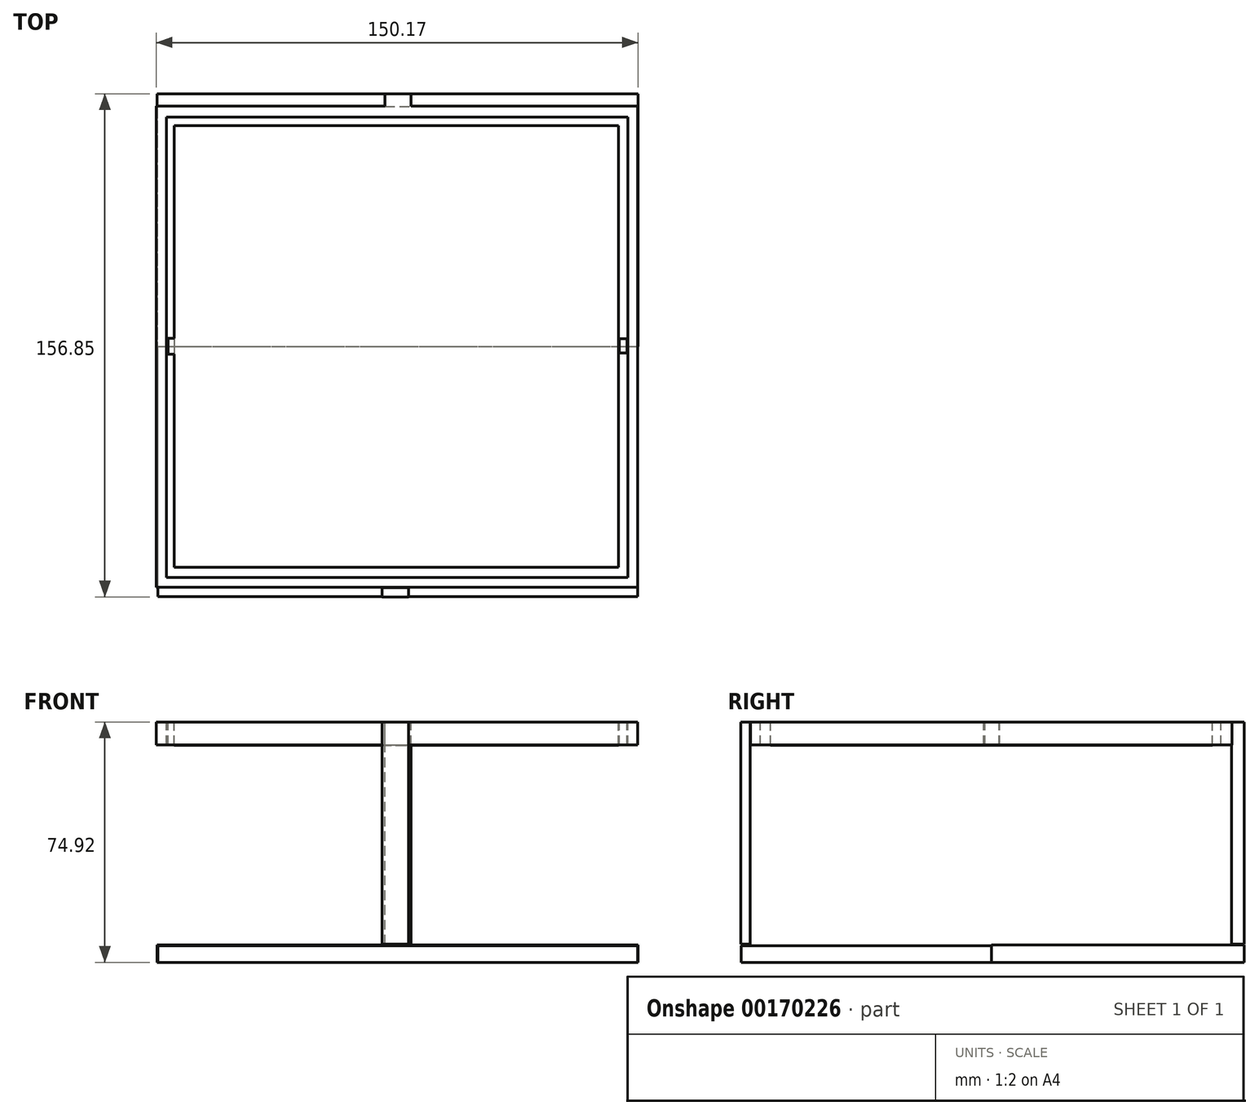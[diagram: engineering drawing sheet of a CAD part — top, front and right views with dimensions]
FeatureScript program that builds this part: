
annotation { "Feature Type Name" : "Feature", "Feature Type Description" : "" }
export const myFeature = defineFeature(function(context is Context, id is Id, definition is map)
    precondition{}
    {
        {
            var Q0;
            Q0=qCreatedBy(makeId("Top.planeOp"),FACE);
            var sketch = newSketch(context, id + "F0", { "sketchPlane" : qUnion([Q0])});
            skLineSegment(sketch, "E0.bottom", {"start": v(-75.11, 74.92) * mm, "end": v(74.92, 74.92) * mm});
            skLineSegment(sketch, "E0.top", {"start": v(-75.11, -75.11) * mm, "end": v(74.92, -75.11) * mm});
            skLineSegment(sketch, "E0.left", {"start": v(-75.11, 74.92) * mm, "end": v(-75.11, -75.11) * mm});
            skLineSegment(sketch, "E0.right", {"start": v(74.92, 74.92) * mm, "end": v(74.92, -75.11) * mm});
            skLineSegment(sketch, "E1.bottom", {"start": v(-71.86, 71.48) * mm, "end": v(71.86, 71.48) * mm});
            skLineSegment(sketch, "E1.top", {"start": v(-71.86, -72.05) * mm, "end": v(71.86, -72.05) * mm});
            skLineSegment(sketch, "E1.left", {"start": v(-71.86, 71.48) * mm, "end": v(-71.86, -72.05) * mm});
            skLineSegment(sketch, "E1.right", {"start": v(71.86, 71.48) * mm, "end": v(71.86, -72.05) * mm});
            skLineSegment(sketch, "E2.bottom", {"start": v(-68.8, 68.99) * mm, "end": v(69.37, 68.99) * mm});
            skLineSegment(sketch, "E2.top", {"start": v(-68.8, -69.18) * mm, "end": v(69.37, -69.18) * mm});
            skLineSegment(sketch, "E2.left", {"start": v(-68.8, 68.99) * mm, "end": v(-68.8, -69.18) * mm});
            skLineSegment(sketch, "E2.right", {"start": v(69.37, 68.99) * mm, "end": v(69.37, -69.18) * mm});
            skLineSegment(sketch, "E3.bottom", {"start": v(-2.58, 71.48) * mm, "end": v(2.58, 71.48) * mm});
            skLineSegment(sketch, "E3.top", {"start": v(-2.58, 68.99) * mm, "end": v(2.58, 68.99) * mm});
            skLineSegment(sketch, "E3.left", {"start": v(-2.58, 71.48) * mm, "end": v(-2.58, 68.99) * mm});
            skLineSegment(sketch, "E3.right", {"start": v(2.58, 71.48) * mm, "end": v(2.58, 68.99) * mm});
            skLineSegment(sketch, "E4.bottom", {"start": v(2.58, -69.18) * mm, "end": v(-2.58, -69.18) * mm});
            skLineSegment(sketch, "E4.top", {"start": v(2.58, -72.05) * mm, "end": v(-2.58, -72.05) * mm});
            skLineSegment(sketch, "E4.left", {"start": v(2.58, -69.18) * mm, "end": v(2.58, -72.05) * mm});
            skLineSegment(sketch, "E4.right", {"start": v(-2.58, -69.18) * mm, "end": v(-2.58, -72.05) * mm});
            skSolve(sketch);
        }
        {
            var Q0;
            Q0 = qSketchRegion(id + "F0", true);
            extrude(context, id + "F1", {"entities" : qUnion([Q0]), "oppositeDirection" : true, "depth" : 7.2 * mm});
        }
        {
            var Q0;
            Q0=qCreatedBy(makeId("Top.planeOp"),FACE);
            var sketch = newSketch(context, id + "F2", { "sketchPlane" : qUnion([Q0])});
            skLineSegment(sketch, "E5.bottom", {"start": v(-69.48, 68.8) * mm, "end": v(68.99, 68.8) * mm});
            skLineSegment(sketch, "E5.top", {"start": v(-69.48, -68.9) * mm, "end": v(68.99, -68.9) * mm});
            skLineSegment(sketch, "E5.left", {"start": v(-69.48, 68.8) * mm, "end": v(-69.48, -68.9) * mm});
            skLineSegment(sketch, "E5.right", {"start": v(68.99, 68.8) * mm, "end": v(68.99, -68.9) * mm});
            skSolve(sketch);
        }
        {
            var Q0;
            Q0 = qSketchRegion(id + "F2", true);
            extrude(context, id + "F3", {"entities" : qUnion([Q0]), "oppositeDirection" : true, "depth" : 7.3 * mm});
        }
        {
            var Q0;
            Q0=qCreatedBy(makeId("Top.planeOp"),FACE);
            var sketch = newSketch(context, id + "F4", { "sketchPlane" : qUnion([Q0])});
            skLineSegment(sketch, "E6.bottom", {"start": v(-71.4, 2.53) * mm, "end": v(-69.48, 2.53) * mm});
            skLineSegment(sketch, "E6.top", {"start": v(-71.4, -2.45) * mm, "end": v(-69.48, -2.45) * mm});
            skLineSegment(sketch, "E6.left", {"start": v(-71.4, 2.53) * mm, "end": v(-71.4, -2.45) * mm});
            skLineSegment(sketch, "E6.right", {"start": v(-69.48, 2.53) * mm, "end": v(-69.48, -2.45) * mm});
            skLineSegment(sketch, "E7.bottom", {"start": v(69.18, 2.34) * mm, "end": v(71.67, 2.34) * mm});
            skLineSegment(sketch, "E7.top", {"start": v(69.18, -2.07) * mm, "end": v(71.67, -2.07) * mm});
            skLineSegment(sketch, "E7.left", {"start": v(69.18, 2.34) * mm, "end": v(69.18, -2.07) * mm});
            skLineSegment(sketch, "E7.right", {"start": v(71.67, 2.34) * mm, "end": v(71.67, -2.07) * mm});
            skSolve(sketch);
        }
        {
            var Q0;
            Q0 = qSketchRegion(id + "F4", true);
            extrude(context, id + "F5", {"entities" : qUnion([Q0]), "operationType" : NewBodyOperationType.ADD, "oppositeDirection" : true, "depth" : 7.2 * mm});
        }
        {
            var Q0;
            Q0=qCreatedBy(makeId("Top.planeOp"),FACE);
            var sketch = newSketch(context, id + "F6", { "sketchPlane" : qUnion([Q0])});
            skLineSegment(sketch, "E8.bottom", {"start": v(-3.8, 74.73) * mm, "end": v(4.25, 74.73) * mm});
            skLineSegment(sketch, "E8.top", {"start": v(-3.8, 78.75) * mm, "end": v(4.25, 78.75) * mm});
            skLineSegment(sketch, "E8.left", {"start": v(-3.8, 74.73) * mm, "end": v(-3.8, 78.75) * mm});
            skLineSegment(sketch, "E8.right", {"start": v(4.25, 74.73) * mm, "end": v(4.25, 78.75) * mm});
            skLineSegment(sketch, "E9.bottom", {"start": v(-4.75, -75.23) * mm, "end": v(3.49, -75.23) * mm});
            skLineSegment(sketch, "E9.top", {"start": v(-4.75, -78.1) * mm, "end": v(3.49, -78.1) * mm});
            skLineSegment(sketch, "E9.left", {"start": v(-4.75, -75.23) * mm, "end": v(-4.75, -78.1) * mm});
            skLineSegment(sketch, "E9.right", {"start": v(3.49, -75.23) * mm, "end": v(3.49, -78.1) * mm});
            skSolve(sketch);
        }
        {
            var Q0;
            Q0 = qSketchRegion(id + "F6", true);
            extrude(context, id + "F7", {"entities" : qUnion([Q0]), "operationType" : NewBodyOperationType.ADD, "oppositeDirection" : true, "depth" : 69.3 * mm});
        }
        {
            var Q0;
            Q0=qCreatedBy(makeId("Front.planeOp"),FACE);
            var sketch = newSketch(context, id + "F8", { "sketchPlane" : qUnion([Q0])});
            skLineSegment(sketch, "E10.bottom", {"start": v(-74.79, -69.56) * mm, "end": v(75.06, -69.56) * mm});
            skLineSegment(sketch, "E10.top", {"start": v(-74.79, -74.92) * mm, "end": v(75.06, -74.92) * mm});
            skLineSegment(sketch, "E10.left", {"start": v(-74.79, -69.56) * mm, "end": v(-74.79, -74.92) * mm});
            skLineSegment(sketch, "E10.right", {"start": v(75.06, -69.56) * mm, "end": v(75.06, -74.92) * mm});
            skSolve(sketch);
        }
        {
            var Q0;
            Q0 = qSketchRegion(id + "F8", true);
            extrude(context, id + "F9", {"entities" : qUnion([Q0]), "oppositeDirection" : true, "depth" : 78.7 * mm});
        }
        {
            var Q0;
            Q0=qCreatedBy(makeId("Front.planeOp"),FACE);
            var sketch = newSketch(context, id + "F10", { "sketchPlane" : qUnion([Q0])});
            skLineSegment(sketch, "E11.bottom", {"start": v(-74.57, -69.76) * mm, "end": v(74.9, -69.76) * mm});
            skLineSegment(sketch, "E11.top", {"start": v(-74.57, -74.92) * mm, "end": v(74.9, -74.92) * mm});
            skLineSegment(sketch, "E11.left", {"start": v(-74.57, -69.76) * mm, "end": v(-74.57, -74.92) * mm});
            skLineSegment(sketch, "E11.right", {"start": v(74.9, -69.76) * mm, "end": v(74.9, -74.92) * mm});
            skSolve(sketch);
        }
        {
            var Q0;
            Q0 = qSketchRegion(id + "F10", true);
            extrude(context, id + "F11", {"entities" : qUnion([Q0]), "operationType" : NewBodyOperationType.ADD, "depth" : 78 * mm});
        }
    });
